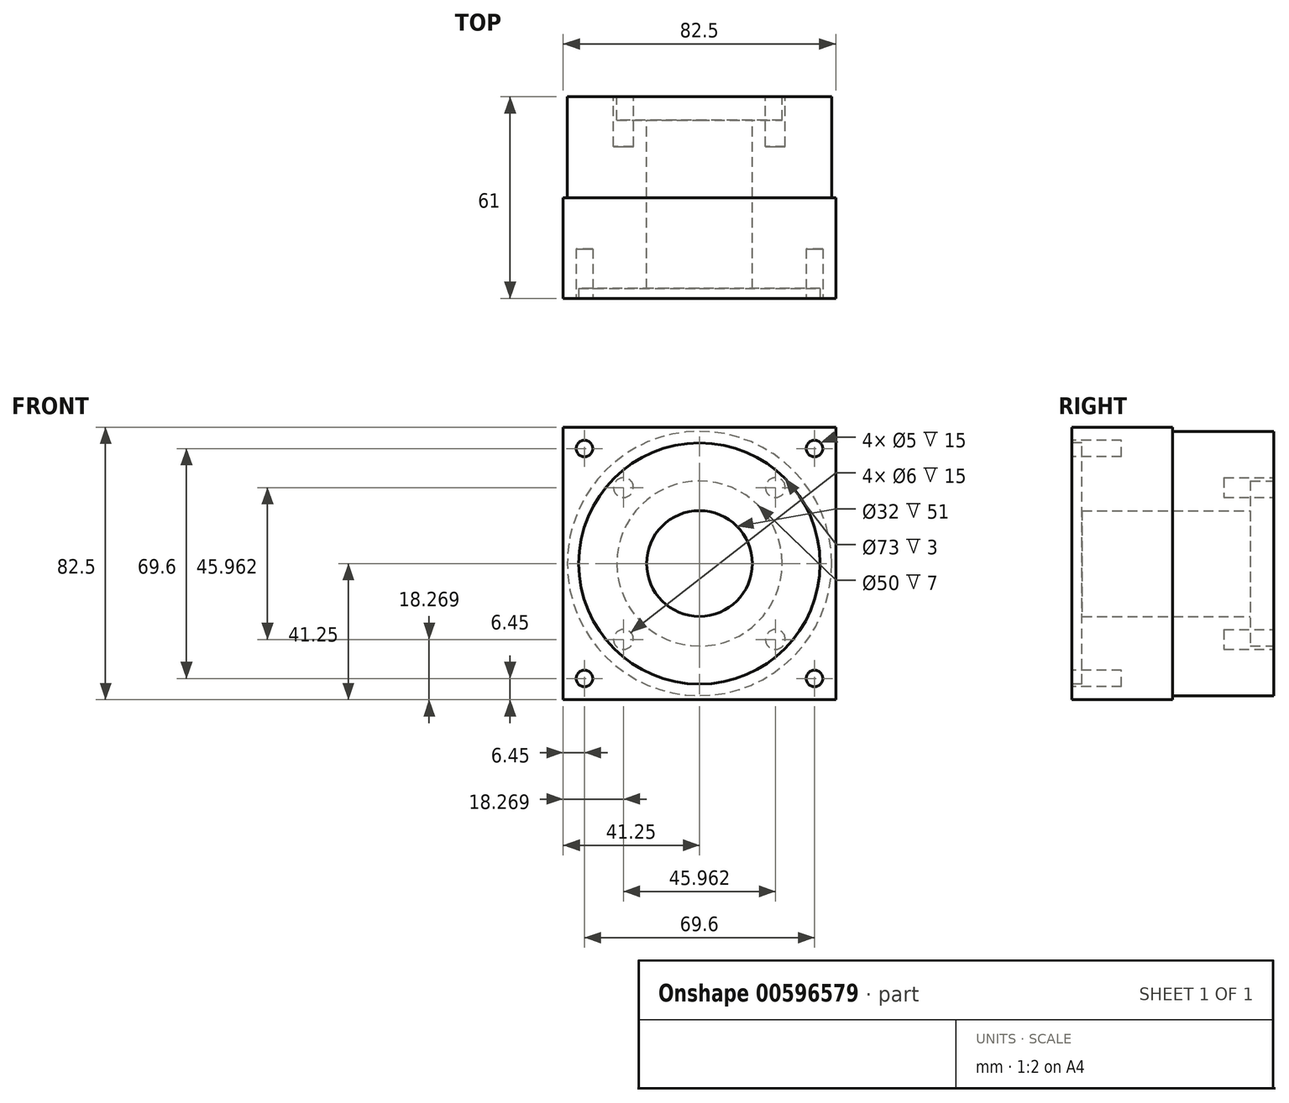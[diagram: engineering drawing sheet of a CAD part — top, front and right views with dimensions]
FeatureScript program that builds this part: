
annotation { "Feature Type Name" : "Feature", "Feature Type Description" : "" }
export const myFeature = defineFeature(function(context is Context, id is Id, definition is map)
    precondition{}
    {
        {
            var Q0;
            Q0=qCreatedBy(makeId("Front.planeOp"),FACE);
            var sketch = newSketch(context, id + "F0", { "sketchPlane" : qUnion([Q0])});
            skCircle(sketch, "E0", {"center": v(0, 0) * mm, "radius": 40 * mm});
            skSolve(sketch);
        }
        {
            var Q0;
            Q0 = qSketchRegion(id + "F0", true);
            extrude(context, id + "F1", {"entities" : qUnion([Q0]), "depth" : 30.5 * mm, "offsetDistance" : 25 * mm});
        }
        {
            var Q0;
            Q0=makeQuery(id+"F1.opExtrude","CAP_FACE",FACE,{"disambiguationData":[OSD([sQuery(id+"F0.wireOp",EDGE,"E0")])],"isStart":false});
            var sketch = newSketch(context, id + "F2", { "sketchPlane" : qUnion([Q0])});
            skLineSegment(sketch, "E1.bottom", {"start": v(-41.25, -41.25) * mm, "end": v(41.25, -41.25) * mm});
            skLineSegment(sketch, "E1.top", {"start": v(-41.25, 41.25) * mm, "end": v(41.25, 41.25) * mm});
            skLineSegment(sketch, "E1.left", {"start": v(-41.25, -41.25) * mm, "end": v(-41.25, 41.25) * mm});
            skLineSegment(sketch, "E1.right", {"start": v(41.25, -41.25) * mm, "end": v(41.25, 41.25) * mm});
            skSolve(sketch);
        }
        {
            var Q0;
            Q0 = qSketchRegion(id + "F2", true);
            extrude(context, id + "F3", {"entities" : qUnion([Q0]), "operationType" : NewBodyOperationType.ADD, "depth" : 30.5 * mm, "offsetDistance" : 25 * mm});
        }
        {
            var Q0;
            Q0=makeQuery(id+"F1.opExtrude","CAP_FACE",FACE,{"disambiguationData":[OSD([sQuery(id+"F0.wireOp",EDGE,"E0")])],"isStart":true});
            var sketch = newSketch(context, id + "F4", { "sketchPlane" : qUnion([Q0])});
            skCircle(sketch, "E2", {"center": v(0, 0) * mm, "radius": 16 * mm});
            skSolve(sketch);
        }
        {
            var Q0;
            Q0=makeQuery(id+"F4.imprint","IMPRINT",FACE,{"disambiguationData":[TD([[makeQuery(id+"F4.imprint","IMPRINT",EDGE,{"derivedFrom":sQuery(id+"F4.wireOp",EDGE,"E2")}),1.0]])]});
            extrude(context, id + "F5", {"entities" : qUnion([Q0]), "operationType" : NewBodyOperationType.REMOVE, "endBound" : BoundingType.THROUGH_ALL, "oppositeDirection" : true, "depth" : 25 * mm, "offsetDistance" : 25 * mm});
        }
        {
            var Q0;
            Q0=makeQuery(id+"F3.opExtrude","CAP_FACE",FACE,{"disambiguationData":[OSD([sQuery(id+"F2.wireOp",EDGE,"E1.bottom"),sQuery(id+"F2.wireOp",EDGE,"E1.top"),sQuery(id+"F2.wireOp",EDGE,"E1.left"),sQuery(id+"F2.wireOp",EDGE,"E1.right")])],"isStart":false});
            var sketch = newSketch(context, id + "F6", { "sketchPlane" : qUnion([Q0])});
            skCircle(sketch, "E3", {"center": v(0, 0) * mm, "radius": 36.5 * mm});
            skCircle(sketch, "E4", {"center": v(109.35, 43.5) * mm, "radius": 2.25 * mm});
            skSolve(sketch);
        }
        {
            var Q0;
            Q0=makeQuery(id+"F6.imprint","IMPRINT",FACE,{"disambiguationData":[TD([[makeQuery(id+"F6.imprint","IMPRINT",EDGE,{"derivedFrom":sQuery(id+"F6.wireOp",EDGE,"E3")}),1.0]])]});
            extrude(context, id + "F7", {"entities" : qUnion([Q0]), "operationType" : NewBodyOperationType.REMOVE, "oppositeDirection" : true, "depth" : 3 * mm, "offsetDistance" : 25 * mm});
        }
        {
            var Q0;
            Q0=makeQuery(id+"F1.opExtrude","CAP_FACE",FACE,{"disambiguationData":[OSD([sQuery(id+"F0.wireOp",EDGE,"E0")])],"isStart":true});
            var sketch = newSketch(context, id + "F8", { "sketchPlane" : qUnion([Q0])});
            skCircle(sketch, "E5", {"center": v(0, 0) * mm, "radius": 25 * mm});
            skSolve(sketch);
        }
        {
            var Q0;
            Q0 = qSketchRegion(id + "F8", true);
            extrude(context, id + "F9", {"entities" : qUnion([Q0]), "operationType" : NewBodyOperationType.REMOVE, "oppositeDirection" : true, "depth" : 7 * mm, "offsetDistance" : 25 * mm});
        }
        {
            var Q0;
            Q0=makeQuery(id+"F3.opExtrude","CAP_FACE",FACE,{"disambiguationData":[OSD([sQuery(id+"F2.wireOp",EDGE,"E1.bottom"),sQuery(id+"F2.wireOp",EDGE,"E1.top"),sQuery(id+"F2.wireOp",EDGE,"E1.left"),sQuery(id+"F2.wireOp",EDGE,"E1.right")])],"isStart":false});
            var sketch = newSketch(context, id + "F10", { "sketchPlane" : qUnion([Q0])});
            skCircle(sketch, "E6", {"center": v(-34.8, 34.8) * mm, "radius": 2.5 * mm});
            skCircle(sketch, "E7", {"center": v(34.8, 34.8) * mm, "radius": 2.5 * mm});
            skCircle(sketch, "E8", {"center": v(34.8, -34.8) * mm, "radius": 2.5 * mm});
            skCircle(sketch, "E9", {"center": v(-34.8, -34.8) * mm, "radius": 2.5 * mm});
            skSolve(sketch);
        }
        {
            var Q0;
            Q0 = qSketchRegion(id + "F10", true);
            extrude(context, id + "F11", {"entities" : qUnion([Q0]), "operationType" : NewBodyOperationType.REMOVE, "oppositeDirection" : true, "depth" : 15 * mm, "offsetDistance" : 25 * mm});
        }
        {
            var Q0;
            Q0=makeQuery(id+"F1.opExtrude","CAP_FACE",FACE,{"disambiguationData":[OSD([sQuery(id+"F0.wireOp",EDGE,"E0")])],"isStart":true});
            var sketch = newSketch(context, id + "F12", { "sketchPlane" : qUnion([Q0])});
            skCircle(sketch, "E10", {"center": v(0, 0) * mm, "radius": 32.5 * mm, "construction": true});
            skLineSegment(sketch, "E11", {"start": v(0, 0) * mm, "end": v(-22.98, 22.98) * mm, "construction": true});
            skCircle(sketch, "E12", {"center": v(-22.98, 22.98) * mm, "radius": 3 * mm});
            skCircle(sketch, "E13.1.0", {"center": v(-22.98, -22.98) * mm, "radius": 3 * mm});
            skCircle(sketch, "E13.2.0", {"center": v(22.98, -22.98) * mm, "radius": 3 * mm});
            skCircle(sketch, "E13.3.0", {"center": v(22.98, 22.98) * mm, "radius": 3 * mm});
            skSolve(sketch);
        }
        {
            var Q0;
            Q0 = qSketchRegion(id + "F12", true);
            extrude(context, id + "F13", {"entities" : qUnion([Q0]), "operationType" : NewBodyOperationType.REMOVE, "oppositeDirection" : true, "depth" : 15 * mm, "offsetDistance" : 25 * mm});
        }
    });
